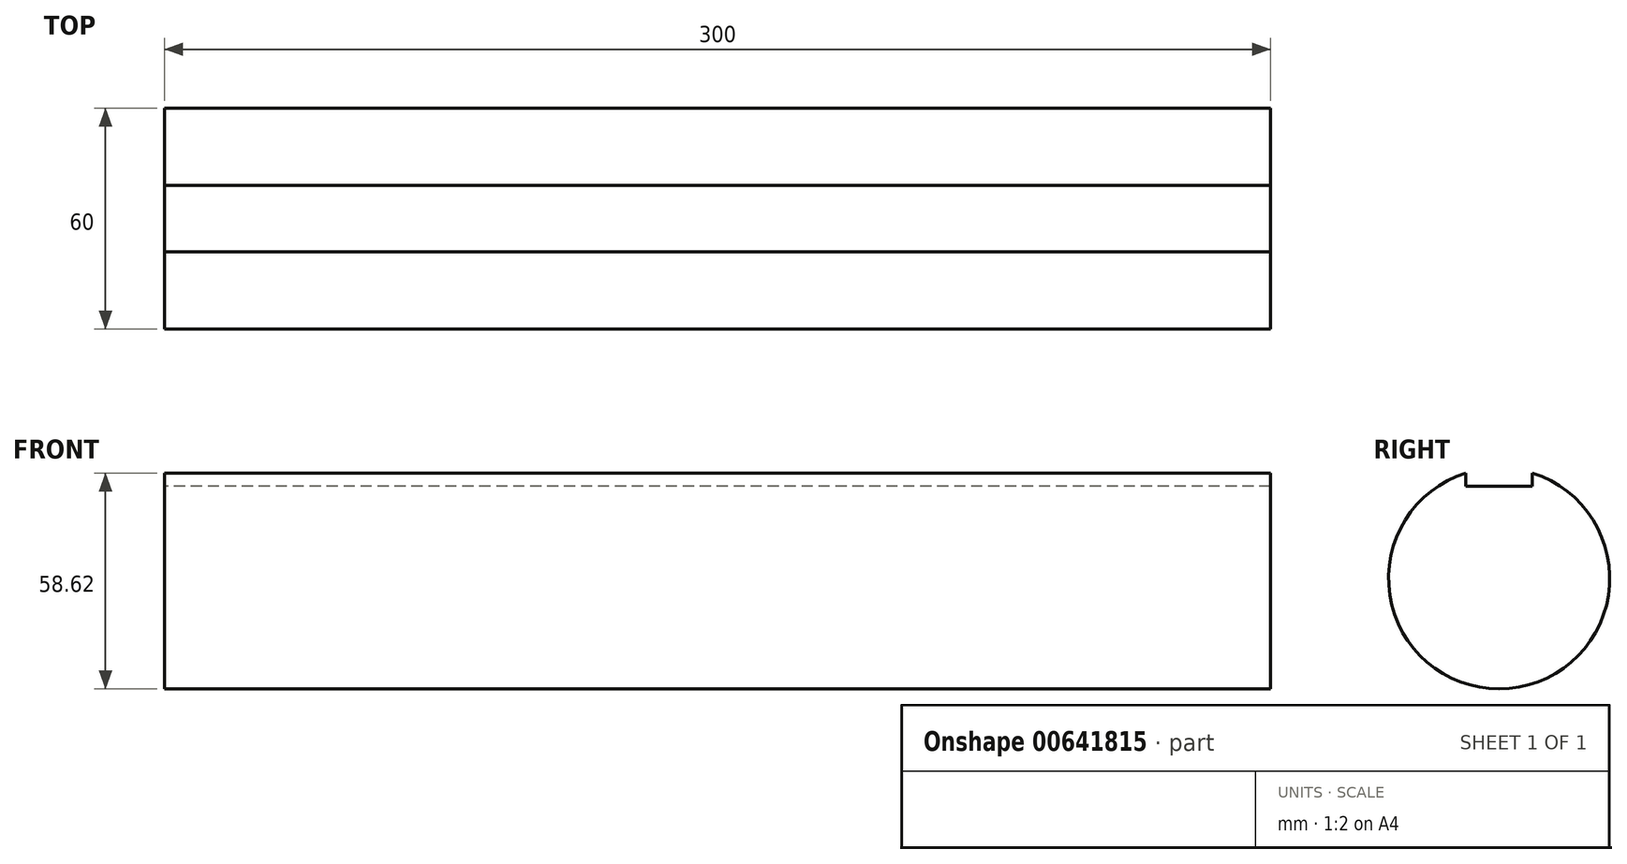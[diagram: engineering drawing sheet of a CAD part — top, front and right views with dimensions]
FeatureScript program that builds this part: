
annotation { "Feature Type Name" : "Feature", "Feature Type Description" : "" }
export const myFeature = defineFeature(function(context is Context, id is Id, definition is map)
    precondition{}
    {
        {
            var Q0;
            Q0=qCreatedBy(makeId("Right.planeOp"),FACE);
            var sketch = newSketch(context, id + "F0", { "sketchPlane" : qUnion([Q0])});
            skCircle(sketch, "E0", {"center": v(0, 0) * mm, "radius": 30 * mm});
            skLineSegment(sketch, "E1", {"start": v(0, 30) * mm, "end": v(0, 25) * mm});
            skLineSegment(sketch, "E2", {"start": v(0, 25) * mm, "end": v(9, 25) * mm});
            skLineSegment(sketch, "E3", {"start": v(9, 25) * mm, "end": v(9, 30) * mm});
            skLineSegment(sketch, "E4.MirrorCS", {"start": v(0, 25) * mm, "end": v(-9, 25) * mm});
            skLineSegment(sketch, "E5", {"start": v(-9, 25) * mm, "end": v(-9, 30) * mm});
            skLineSegment(sketch, "E6", {"start": v(-9, 30) * mm, "end": v(9, 30) * mm});
            skSolve(sketch);
        }
        {
            var Q0;
            {var subQ6=sQuery(id+"F0.wireOp",EDGE,"E2");Q0=makeQuery(id+"F0.imprint","IMPRINT",FACE,{"disambiguationData":[TD([[makeQuery(id+"F0.imprint","IMPRINT",EDGE,{"derivedFrom":subQ6}),-1.0]])]});}
            var Q1;
            Q1=sQuery(id+"F0.wireOp",EDGE,"E0");
            extrude(context, id + "F1", {"entities" : qUnion([Q0]), "surfaceEntities" : qUnion([Q1]), "depth" : 300 * mm, "offsetDistance" : 25 * mm});
        }
    });
